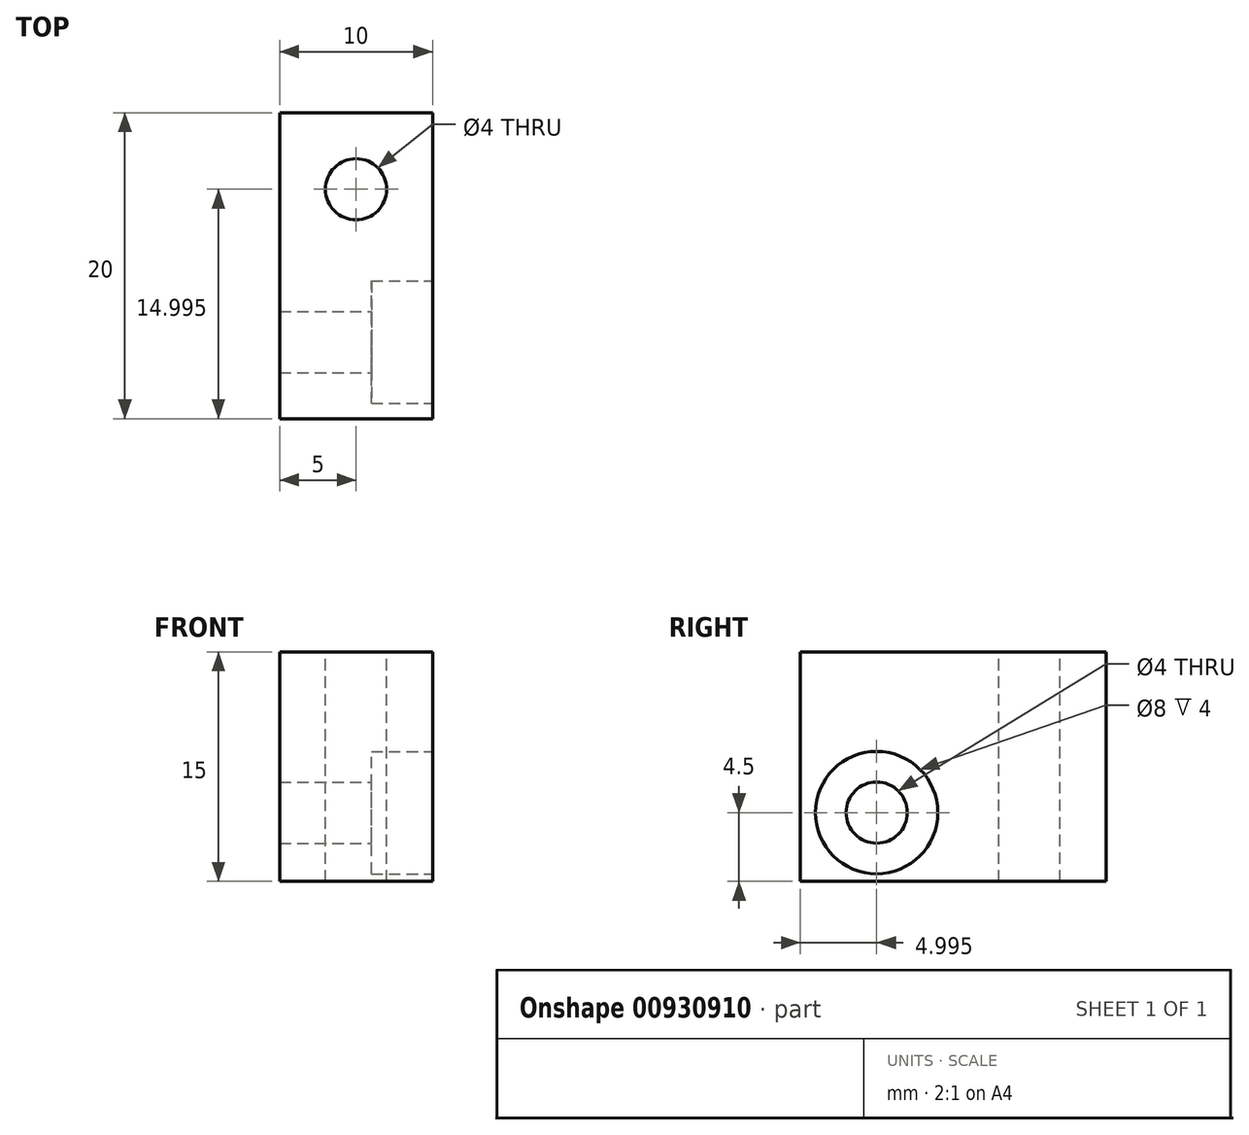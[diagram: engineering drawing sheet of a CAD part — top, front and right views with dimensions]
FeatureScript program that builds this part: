
annotation { "Feature Type Name" : "Feature", "Feature Type Description" : "" }
export const myFeature = defineFeature(function(context is Context, id is Id, definition is map)
    precondition{}
    {
        {
            var Q0;
            Q0=qCreatedBy(makeId("Top.planeOp"),FACE);
            var sketch = newSketch(context, id + "F0", { "sketchPlane" : qUnion([Q0])});
            skLineSegment(sketch, "E0.bottom", {"start": v(-5.85, 14.18) * mm, "end": v(4.15, 14.18) * mm});
            skLineSegment(sketch, "E0.top", {"start": v(-5.85, -5.82) * mm, "end": v(4.15, -5.82) * mm});
            skLineSegment(sketch, "E0.left", {"start": v(-5.85, 14.18) * mm, "end": v(-5.85, -5.82) * mm});
            skLineSegment(sketch, "E0.right", {"start": v(4.15, 14.18) * mm, "end": v(4.15, -5.82) * mm});
            skSolve(sketch);
        }
        {
            var Q0;
            Q0=makeQuery(id+"F0.imprint","IMPRINT",FACE,{"disambiguationData":[TD([[makeQuery(id+"F0.imprint","IMPRINT",EDGE,{"derivedFrom":sQuery(id+"F0.wireOp",EDGE,"E0.bottom")}),-1.0]])]});
            extrude(context, id + "F1", {"entities" : qUnion([Q0]), "depth" : 15 * mm, "offsetDistance" : 25 * mm});
        }
        {
            var Q0;
            Q0=makeQuery(id+"F1.opExtrude","SWEPT_FACE",FACE,{"disambiguationData":[OSD([sQuery(id+"F0.wireOp",EDGE,"E0.right")])]});
            var sketch = newSketch(context, id + "F2", { "sketchPlane" : qUnion([Q0])});
            skCircle(sketch, "E1", {"center": v(-0.82, 4.5) * mm, "radius": 4 * mm});
            skCircle(sketch, "E2", {"center": v(-0.82, 4.5) * mm, "radius": 2 * mm});
            skSolve(sketch);
        }
        {
            var Q0;
            Q0=makeQuery(id+"F2.imprint","IMPRINT",FACE,{"disambiguationData":[TD([[makeQuery(id+"F2.imprint","IMPRINT",EDGE,{"derivedFrom":sQuery(id+"F2.wireOp",EDGE,"E2")}),1.0]])]});
            extrude(context, id + "F3", {"entities" : qUnion([Q0]), "operationType" : NewBodyOperationType.REMOVE, "oppositeDirection" : true, "depth" : 20 * mm, "offsetDistance" : 25 * mm});
        }
        {
            var Q0;
            Q0=makeQuery(id+"F2.imprint","IMPRINT",FACE,{"disambiguationData":[TD([[makeQuery(id+"F2.imprint","IMPRINT",EDGE,{"derivedFrom":sQuery(id+"F2.wireOp",EDGE,"E1")}),1.0]])]});
            var Q1;
            Q1=sQuery(id+"F2.wireOp",EDGE,"E1");
            extrude(context, id + "F4", {"entities" : qUnion([Q0]), "operationType" : NewBodyOperationType.REMOVE, "surfaceEntities" : qUnion([Q1]), "oppositeDirection" : true, "depth" : 4 * mm, "offsetDistance" : 25 * mm});
        }
        {
            var Q0;
            Q0=makeQuery(id+"F1.opExtrude","CAP_FACE",FACE,{"disambiguationData":[OSD([sQuery(id+"F0.wireOp",EDGE,"E0.bottom"),sQuery(id+"F0.wireOp",EDGE,"E0.top"),sQuery(id+"F0.wireOp",EDGE,"E0.left"),sQuery(id+"F0.wireOp",EDGE,"E0.right")])],"isStart":false});
            var sketch = newSketch(context, id + "F5", { "sketchPlane" : qUnion([Q0])});
            skCircle(sketch, "E3", {"center": v(-0.85, 9.18) * mm, "radius": 2 * mm});
            skSolve(sketch);
        }
        {
            var Q0;
            Q0=makeQuery(id+"F5.imprint","IMPRINT",FACE,{"disambiguationData":[TD([[makeQuery(id+"F5.imprint","IMPRINT",EDGE,{"derivedFrom":sQuery(id+"F5.wireOp",EDGE,"E3")}),1.0]])]});
            var Q1;
            Q1=sQuery(id+"F5.wireOp",EDGE,"E3");
            extrude(context, id + "F6", {"entities" : qUnion([Q0]), "operationType" : NewBodyOperationType.REMOVE, "surfaceEntities" : qUnion([Q1]), "oppositeDirection" : true, "depth" : 20 * mm, "offsetDistance" : 25 * mm});
        }
    });
